# Revit family: Casement_30.5_B_Side_Hung_Standard
name_source: partatom
category: Windows
revit_build: Autodesk Revit 2014 (Build: 20130308_1515(x64)
units: mm (PartAtom-declared; Revit-internal decimal feet)

## types (18) — shared parameters
Aluminium Thickness = 1 mm  [stored 0.00328084 ft]
Bead SG Gap = 13 mm  [stored 0.0426509 ft]
Casement Dimension = 31 mm
Custom Sash Width = 554 mm  [stored 1.81759 ft]
DG Extrusion Start = 5 mm  [stored 0.0164042 ft]
DG Gasket Finish = Double Glazing Gasket Material
DG Thickness = 3 mm  [stored 0.00984252 ft]
DG Thickness Calc = 3 mm  [stored 0.00984252 ft]
Default Sill Height = 800 mm  [stored 2.62467 ft]
Depth Bead = 17 mm
Description = Window 30.5mm, Type B side hung
Double Glazing = No
Frame Center Offset = 15 mm  [stored 0.0492126 ft]
Limit Fixed Panel Width Max = 1500 mm
Limit Fixed Panel Width Min = 200 mm  [stored 0.656168 ft]
Limit Sash Height Max = 1200 mm
Limit Sash Height Min = 300 mm  [stored 0.984252 ft]
Limit Sash Width Max = 600 mm  [stored 1.9685 ft]
Limit Sash Width Min = 300 mm  [stored 0.984252 ft]
Limit Window Height Max = 1246 mm
Limit Window Height Min = 346 mm
Limit Window Width Max = 2129 mm
Limit Window Width Min = 829 mm  [stored 2.71982 ft]
Manufacturer = Crealco
Max System DG One Piece Thickness = 3 mm  [stored 0.00984252 ft]
Max System DG Unit Thickness = 18 mm  [stored 0.0590551 ft]
Model = Casement 30.5
Offset Bead SG Center Reversed = 15 mm  [stored 0.0492126 ft]
Offset Mullion Left = 569 mm  [stored 1.8668 ft]
Offset Panel 4 Left = 599 mm  [stored 1.96522 ft]
Offset Sash Left = 23 mm  [stored 0.0754593 ft]
Offset Sash Top = 23 mm  [stored 0.0754593 ft]
Offset Window Exterior = 15 mm  [stored 0.0492126 ft]
SG Gasket Thickness = 6 mm  [stored 0.019685 ft]
Sash Center Offset = 12 mm  [stored 0.0393701 ft]
Sash Overlap = 7 mm  [stored 0.0229659 ft]
Sash Spacing Inner = 8 mm  [stored 0.0262467 ft]
URL = http://www.crealco.co.za
Wall Closure = By host
Width Bead = 15 mm  [stored 0.0492126 ft]
Width Panel 1 = 539 mm  [stored 1.76837 ft]
Width Profile = 30 mm  [stored 0.0984252 ft]
Width Sash = 524 mm  [stored 1.71916 ft]
Width Sash Opening = 554 mm  [stored 1.81759 ft]
zero-valued in all types: Window Exterior Offset

## per-type parameters (varying)
| type | Area Pane Left | Area Pane Right | Clearvue SHGC Value | Clearvue U Value | Custom Windload | Custom Window Height | Custom Window Width | Depth Mullion | Energy Advantage SHGC Value | Energy Advantage U Value | Height | Height Panel 4 | Height Sash | Height Sash Opening | Intruderprufe LowE SHGC Value | Intruderprufe LowE U Value | Intruderprufe SHGC Value | Intruderprufe U Value | Length Mullion | Max Pane Area | Mullion Depth Windload Based | Width | Width Panel 4 | Windload Design |
| 305-0909S-1000Pa | 0.37 m² | 0.21 m² | 0.566 | 6.25 | 1000 mm  [stored 3.28084 ft] | 890 mm  [stored 2.91995 ft] | 890 mm  [stored 2.91995 ft] | 32 mm | 0.506 | 4.81 | 890 mm  [stored 2.91995 ft] | 830 mm  [stored 2.7231 ft] | 814 mm  [stored 2.6706 ft] | 844 mm  [stored 2.76903 ft] | 0.478 | 4.7 | 0.54 | 6.11 | 890 mm  [stored 2.91995 ft] | 0.37 m² | 32 mm | 890 mm  [stored 2.91995 ft] | 261 mm  [stored 0.856299 ft] | 1000 mm  [stored 3.28084 ft] |
| 305-1209S-1000Pa | 0.37 m² | 0.45 m² | 0.613 | 6.17 | 1000 mm  [stored 3.28084 ft] | 890 mm  [stored 2.91995 ft] | 1190 mm  [stored 3.9042 ft] | 32 mm | 0.549 | 4.62 | 890 mm  [stored 2.91995 ft] | 830 mm  [stored 2.7231 ft] | 814 mm  [stored 2.6706 ft] | 844 mm  [stored 2.76903 ft] | 0.517 | 4.51 | 0.585 | 6.04 | 890 mm  [stored 2.91995 ft] | 0.45 m² | 32 mm | 1190 mm  [stored 3.9042 ft] | 561 mm | 1000 mm  [stored 3.28084 ft] |
| 305-1509S-1000Pa | 0.37 m² | 0.7 m² | 0.642 | 6.13 | 1000 mm  [stored 3.28084 ft] | 890 mm  [stored 2.91995 ft] | 1490 mm | 32 mm | 0.574 | 4.5 | 890 mm  [stored 2.91995 ft] | 830 mm  [stored 2.7231 ft] | 814 mm  [stored 2.6706 ft] | 844 mm  [stored 2.76903 ft] | 0.54 | 4.4 | 0.612 | 5.99 | 890 mm  [stored 2.91995 ft] | 0.7 m² | 32 mm | 1490 mm | 861 mm  [stored 2.8248 ft] | 1000 mm  [stored 3.28084 ft] |
| 305-0912S-1000Pa | 0.52 m² | 0.28 m² | 0.59 | 6.24 | 1000 mm  [stored 3.28084 ft] | 1190 mm  [stored 3.9042 ft] | 890 mm  [stored 2.91995 ft] | 32 mm | 0.529 | 4.86 | 1190 mm  [stored 3.9042 ft] | 1130 mm  [stored 3.70735 ft] | 1114 mm  [stored 3.65486 ft] | 1144 mm | 0.499 | 4.75 | 0.561 | 6.1 | 1190 mm  [stored 3.9042 ft] | 0.52 m² | 32 mm | 890 mm  [stored 2.91995 ft] | 261 mm  [stored 0.856299 ft] | 1000 mm  [stored 3.28084 ft] |
| 305-1212S-1000Pa | 0.52 m² | 0.62 m² | 0.637 | 6.16 | 1000 mm  [stored 3.28084 ft] | 1190 mm  [stored 3.9042 ft] | 1190 mm  [stored 3.9042 ft] | 32 mm | 0.569 | 4.53 | 1190 mm  [stored 3.9042 ft] | 1130 mm  [stored 3.70735 ft] | 1114 mm  [stored 3.65486 ft] | 1144 mm | 0.536 | 4.43 | 0.607 | 6.02 | 1190 mm  [stored 3.9042 ft] | 0.62 m² | 32 mm | 1190 mm  [stored 3.9042 ft] | 561 mm | 1000 mm  [stored 3.28084 ft] |
| 305-1512S-1000Pa | 0.52 m² | 0.95 m² | 0.666 | 6.11 | 1000 mm  [stored 3.28084 ft] | 1190 mm  [stored 3.9042 ft] | 1490 mm | 54 mm  [stored 0.177165 ft] | 0.596 | 4.5 | 1190 mm  [stored 3.9042 ft] | 1130 mm  [stored 3.70735 ft] | 1114 mm  [stored 3.65486 ft] | 1144 mm | 0.56 | 4.4 | 0.634 | 5.97 | 1190 mm  [stored 3.9042 ft] | 0.95 m² | 54 mm  [stored 0.177165 ft] | 1490 mm | 861 mm  [stored 2.8248 ft] | 1000 mm  [stored 3.28084 ft] |
| 305-1212S-1500Pa | 0.52 m² | 0.62 m² | 0.638 | 6.16 | 1500 mm | 1190 mm  [stored 3.9042 ft] | 1190 mm  [stored 3.9042 ft] | 54 mm  [stored 0.177165 ft] | 0.571 | 4.63 | 1190 mm  [stored 3.9042 ft] | 1130 mm  [stored 3.70735 ft] | 1114 mm  [stored 3.65486 ft] | 1144 mm | 0.537 | 4.53 | 0.606 | 6.02 | 1190 mm  [stored 3.9042 ft] | 0.62 m² | 54 mm  [stored 0.177165 ft] | 1190 mm  [stored 3.9042 ft] | 561 mm | 1500 mm |
| 305-0909S-1500Pa | 0.37 m² | 0.21 m² | 0.566 | 6.25 | 1500 mm | 890 mm  [stored 2.91995 ft] | 890 mm  [stored 2.91995 ft] | 32 mm | 0.506 | 4.81 | 890 mm  [stored 2.91995 ft] | 830 mm  [stored 2.7231 ft] | 814 mm  [stored 2.6706 ft] | 844 mm  [stored 2.76903 ft] | 0.478 | 4.7 | 0.54 | 6.11 | 890 mm  [stored 2.91995 ft] | 0.37 m² | 32 mm | 890 mm  [stored 2.91995 ft] | 261 mm  [stored 0.856299 ft] | 1500 mm |
| 305-0909S-2000Pa | 0.37 m² | 0.21 m² | 0.566 | 6.25 | 2000 mm | 890 mm  [stored 2.91995 ft] | 890 mm  [stored 2.91995 ft] | 32 mm | 0.506 | 4.81 | 890 mm  [stored 2.91995 ft] | 830 mm  [stored 2.7231 ft] | 814 mm  [stored 2.6706 ft] | 844 mm  [stored 2.76903 ft] | 0.478 | 4.7 | 0.54 | 6.11 | 890 mm  [stored 2.91995 ft] | 0.37 m² | 32 mm | 890 mm  [stored 2.91995 ft] | 261 mm  [stored 0.856299 ft] | 2000 mm |
| 305-0912S-1500Pa | 0.52 m² | 0.28 m² | 0.59 | 6.24 | 1500 mm | 1190 mm  [stored 3.9042 ft] | 890 mm  [stored 2.91995 ft] | 54 mm  [stored 0.177165 ft] | 0.529 | 4.86 | 1190 mm  [stored 3.9042 ft] | 1130 mm  [stored 3.70735 ft] | 1114 mm  [stored 3.65486 ft] | 1144 mm | 0.499 | 4.75 | 0.561 | 6.1 | 1190 mm  [stored 3.9042 ft] | 0.52 m² | 54 mm  [stored 0.177165 ft] | 890 mm  [stored 2.91995 ft] | 261 mm  [stored 0.856299 ft] | 1500 mm |
| 305-0912S-2000Pa | 0.52 m² | 0.28 m² | 0.59 | 6.24 | 2000 mm | 1190 mm  [stored 3.9042 ft] | 890 mm  [stored 2.91995 ft] | 54 mm  [stored 0.177165 ft] | 0.529 | 4.86 | 1190 mm  [stored 3.9042 ft] | 1130 mm  [stored 3.70735 ft] | 1114 mm  [stored 3.65486 ft] | 1144 mm | 0.499 | 4.75 | 0.561 | 6.1 | 1190 mm  [stored 3.9042 ft] | 0.52 m² | 54 mm  [stored 0.177165 ft] | 890 mm  [stored 2.91995 ft] | 261 mm  [stored 0.856299 ft] | 2000 mm |
| 305-1209S-1500Pa | 0.37 m² | 0.45 m² | 0.613 | 6.17 | 1500 mm | 890 mm  [stored 2.91995 ft] | 1190 mm  [stored 3.9042 ft] | 32 mm | 0.549 | 4.62 | 890 mm  [stored 2.91995 ft] | 830 mm  [stored 2.7231 ft] | 814 mm  [stored 2.6706 ft] | 844 mm  [stored 2.76903 ft] | 0.517 | 4.51 | 0.585 | 6.04 | 890 mm  [stored 2.91995 ft] | 0.45 m² | 32 mm | 1190 mm  [stored 3.9042 ft] | 561 mm | 1500 mm |
| 305-1209S-2000Pa | 0.37 m² | 0.45 m² | 0.613 | 6.17 | 2000 mm | 890 mm  [stored 2.91995 ft] | 1190 mm  [stored 3.9042 ft] | 32 mm | 0.549 | 4.62 | 890 mm  [stored 2.91995 ft] | 830 mm  [stored 2.7231 ft] | 814 mm  [stored 2.6706 ft] | 844 mm  [stored 2.76903 ft] | 0.517 | 4.51 | 0.585 | 6.04 | 890 mm  [stored 2.91995 ft] | 0.45 m² | 32 mm | 1190 mm  [stored 3.9042 ft] | 561 mm | 2000 mm |
| 305-1212S-2000Pa | 0.52 m² | 0.62 m² | 0.638 | 6.16 | 2000 mm | 1190 mm  [stored 3.9042 ft] | 1190 mm  [stored 3.9042 ft] | 54 mm  [stored 0.177165 ft] | 0.571 | 4.63 | 1190 mm  [stored 3.9042 ft] | 1130 mm  [stored 3.70735 ft] | 1114 mm  [stored 3.65486 ft] | 1144 mm | 0.537 | 4.53 | 0.606 | 6.02 | 1190 mm  [stored 3.9042 ft] | 0.62 m² | 54 mm  [stored 0.177165 ft] | 1190 mm  [stored 3.9042 ft] | 561 mm | 2000 mm |
| 305-1509S-1500Pa | 0.37 m² | 0.7 m² | 0.642 | 6.13 | 1500 mm | 890 mm  [stored 2.91995 ft] | 1490 mm | 32 mm | 0.574 | 4.5 | 890 mm  [stored 2.91995 ft] | 830 mm  [stored 2.7231 ft] | 814 mm  [stored 2.6706 ft] | 844 mm  [stored 2.76903 ft] | 0.54 | 4.4 | 0.612 | 5.99 | 890 mm  [stored 2.91995 ft] | 0.7 m² | 32 mm | 1490 mm | 861 mm  [stored 2.8248 ft] | 1500 mm |
| 305-1509S-2000Pa | 0.37 m² | 0.7 m² | 0.642 | 6.13 | 2000 mm | 890 mm  [stored 2.91995 ft] | 1490 mm | 32 mm | 0.574 | 4.5 | 890 mm  [stored 2.91995 ft] | 830 mm  [stored 2.7231 ft] | 814 mm  [stored 2.6706 ft] | 844 mm  [stored 2.76903 ft] | 0.54 | 4.4 | 0.612 | 5.99 | 890 mm  [stored 2.91995 ft] | 0.7 m² | 32 mm | 1490 mm | 861 mm  [stored 2.8248 ft] | 2000 mm |
| 305-1512S-1500Pa | 0.52 m² | 0.95 m² | 0.666 | 6.11 | 1500 mm | 1190 mm  [stored 3.9042 ft] | 1490 mm | 54 mm  [stored 0.177165 ft] | 0.596 | 4.5 | 1190 mm  [stored 3.9042 ft] | 1130 mm  [stored 3.70735 ft] | 1114 mm  [stored 3.65486 ft] | 1144 mm | 0.56 | 4.4 | 0.634 | 5.97 | 1190 mm  [stored 3.9042 ft] | 0.95 m² | 54 mm  [stored 0.177165 ft] | 1490 mm | 861 mm  [stored 2.8248 ft] | 1500 mm |
| 305-1512S-2000Pa | 0.52 m² | 0.95 m² | 0.666 | 6.11 | 2000 mm | 1190 mm  [stored 3.9042 ft] | 1490 mm | 54 mm  [stored 0.177165 ft] | 0.596 | 4.5 | 1190 mm  [stored 3.9042 ft] | 1130 mm  [stored 3.70735 ft] | 1114 mm  [stored 3.65486 ft] | 1144 mm | 0.56 | 4.4 | 0.634 | 5.97 | 1190 mm  [stored 3.9042 ft] | 0.95 m² | 54 mm  [stored 0.177165 ft] | 1490 mm | 861 mm  [stored 2.8248 ft] | 2000 mm |

note: [stored X ft] marks values corroborated as IEEE doubles in the binary element streams (Revit-internal decimal feet)

## geometry (parser evidence)
native form markers: Extrusion x1, Sweep x28
no freeform markers — native parametric forms only
